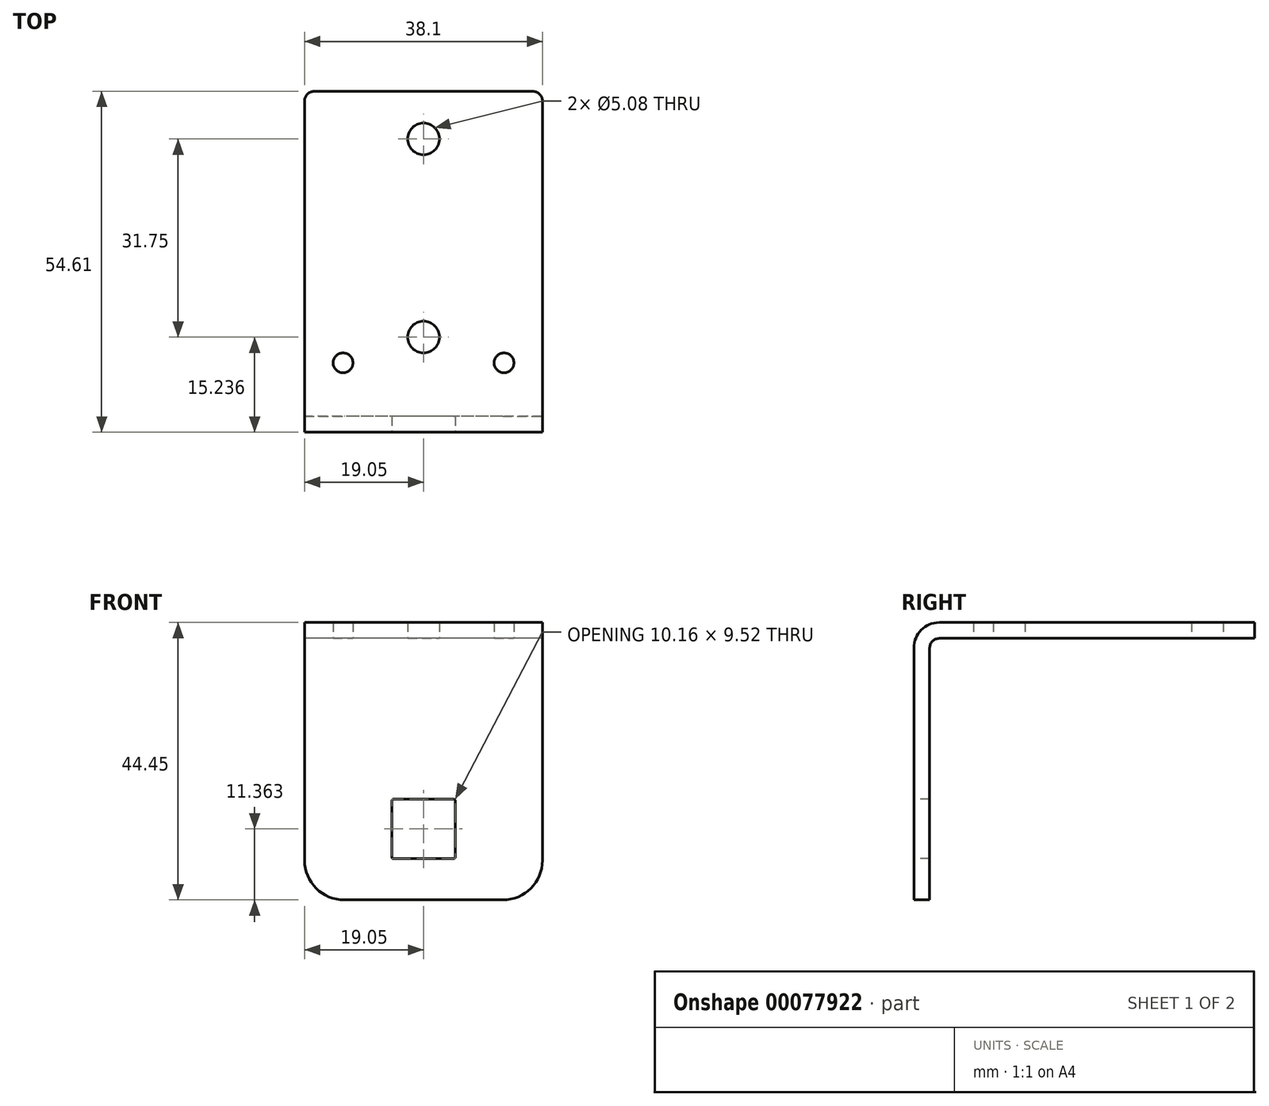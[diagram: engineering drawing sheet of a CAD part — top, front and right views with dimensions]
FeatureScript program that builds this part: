
annotation { "Feature Type Name" : "Feature", "Feature Type Description" : "" }
export const myFeature = defineFeature(function(context is Context, id is Id, definition is map)
    precondition{}
    {
        {
            var Q0;
            Q0=qCreatedBy(makeId("Right.planeOp"),FACE);
            var sketch = newSketch(context, id + "F0", { "sketchPlane" : qUnion([Q0])});
            skLineSegment(sketch, "E0.bottom", {"start": v(-52.32, 1.02) * mm, "end": v(-54.86, 1.02) * mm});
            skLineSegment(sketch, "E0.top", {"start": v(-0.25, 45.47) * mm, "end": v(-50.8, 45.47) * mm});
            skLineSegment(sketch, "E0.left", {"start": v(-0.25, 42.93) * mm, "end": v(-0.25, 45.47) * mm});
            skLineSegment(sketch, "E0.right", {"start": v(-54.86, 1.02) * mm, "end": v(-54.86, 41.4) * mm});
            skLineSegment(sketch, "E1", {"start": v(-52.32, 1.02) * mm, "end": v(-52.32, 41.4) * mm});
            skLineSegment(sketch, "E2", {"start": v(-50.8, 42.93) * mm, "end": v(-0.25, 42.93) * mm});
            skPoint(sketch, "E3.visualSharp", {"position": v(-52.32, 42.93) * mm});
            skArc(sketch, "E3.filletArc", {"start": v(-50.8, 42.93) * mm, "mid": v(-51.88, 42.48) * mm, "end": v(-52.32, 41.4) * mm});
            skPoint(sketch, "E4.visualSharp", {"position": v(-54.86, 45.47) * mm});
            skArc(sketch, "E4.filletArc", {"start": v(-50.8, 45.47) * mm, "mid": v(-53.67, 44.28) * mm, "end": v(-54.86, 41.4) * mm});
            skSolve(sketch);
        }
        {
            var Q0;
            Q0 = qSketchRegion(id + "F0", true);
            extrude(context, id + "F1", {"entities" : qUnion([Q0]), "depth" : 38.1 * mm});
        }
        {
            var Q0;
            Q0=makeQuery(id+"F1.opExtrude","CAP_EDGE",EDGE,{"disambiguationData":[OSD([sQuery(id+"F0.wireOp",EDGE,"E0.left")])],"isStart":true});
            var Q1;
            Q1=makeQuery(id+"F1.opExtrude","CAP_EDGE",EDGE,{"disambiguationData":[OSD([sQuery(id+"F0.wireOp",EDGE,"E0.left")])],"isStart":false});
            fillet(context, id + "F2", {"entities" : qUnion([Q0, Q1]), "radius" : 1.52 * mm, "tangentPropagation" : true, "allowEdgeOverflow" : false});
        }
        {
            var Q0;
            Q0=makeQuery(id+"F1.opExtrude","SWEPT_FACE",FACE,{"disambiguationData":[OSD([sQuery(id+"F0.wireOp",EDGE,"E2")])]});
            var sketch = newSketch(context, id + "F3", { "sketchPlane" : qUnion([Q0])});
            skCircle(sketch, "E5", {"center": v(6.16, 43.75) * mm, "radius": 1.59 * mm});
            skCircle(sketch, "E6", {"center": v(19.05, 39.62) * mm, "radius": 2.54 * mm});
            skCircle(sketch, "E7", {"center": v(31.94, 43.75) * mm, "radius": 1.59 * mm});
            skCircle(sketch, "E8", {"center": v(19.05, 7.87) * mm, "radius": 2.54 * mm});
            skLineSegment(sketch, "E9", {"start": v(19.05, 0.25) * mm, "end": v(19.05, 50.8) * mm, "construction": true});
            skLineSegment(sketch, "E10", {"start": v(0, 43.75) * mm, "end": v(38.1, 43.75) * mm, "construction": true});
            skSolve(sketch);
        }
        {
            var Q0;
            Q0 = qSketchRegion(id + "F3", true);
            extrude(context, id + "F4", {"entities" : qUnion([Q0]), "operationType" : NewBodyOperationType.REMOVE, "endBound" : BoundingType.UP_TO_NEXT, "oppositeDirection" : true, "depth" : 25.4 * mm});
        }
        {
            var Q0;
            Q0=makeQuery(id+"F1.opExtrude","SWEPT_FACE",FACE,{"disambiguationData":[OSD([sQuery(id+"F0.wireOp",EDGE,"E0.right")])]});
            var sketch = newSketch(context, id + "F5", { "sketchPlane" : qUnion([Q0])});
            skLineSegment(sketch, "E11.bottom", {"start": v(14.22, 7.62) * mm, "end": v(23.88, 7.62) * mm});
            skLineSegment(sketch, "E11.top", {"start": v(14.22, 17.15) * mm, "end": v(23.88, 17.15) * mm});
            skLineSegment(sketch, "E11.left", {"start": v(13.97, 7.87) * mm, "end": v(13.97, 16.9) * mm});
            skLineSegment(sketch, "E11.right", {"start": v(24.13, 7.87) * mm, "end": v(24.13, 16.9) * mm});
            skLineSegment(sketch, "E12", {"start": v(19.05, 1.02) * mm, "end": v(19.05, 7.62) * mm, "construction": true});
            skPoint(sketch, "E13.visualSharp", {"position": v(13.97, 17.15) * mm});
            skArc(sketch, "E13.filletArc", {"start": v(14.22, 17.14) * mm, "mid": v(14.04, 17.07) * mm, "end": v(13.97, 16.9) * mm});
            skPoint(sketch, "E14.visualSharp", {"position": v(24.13, 17.15) * mm});
            skArc(sketch, "E14.filletArc", {"start": v(24.13, 16.9) * mm, "mid": v(24.06, 17.07) * mm, "end": v(23.88, 17.15) * mm});
            skPoint(sketch, "E15.visualSharp", {"position": v(24.13, 7.62) * mm});
            skArc(sketch, "E15.filletArc", {"start": v(23.88, 7.62) * mm, "mid": v(24.06, 7.7) * mm, "end": v(24.13, 7.87) * mm});
            skPoint(sketch, "E16.visualSharp", {"position": v(13.97, 7.62) * mm});
            skArc(sketch, "E16.filletArc", {"start": v(13.97, 7.87) * mm, "mid": v(14.04, 7.7) * mm, "end": v(14.22, 7.62) * mm});
            skSolve(sketch);
        }
        {
            var Q0;
            Q0 = qSketchRegion(id + "F5", true);
            extrude(context, id + "F6", {"entities" : qUnion([Q0]), "operationType" : NewBodyOperationType.REMOVE, "endBound" : BoundingType.UP_TO_NEXT, "oppositeDirection" : true, "depth" : 25.4 * mm});
        }
        {
            var Q0;
            Q0=makeQuery(id+"F1.opExtrude","CAP_EDGE",EDGE,{"disambiguationData":[OSD([sQuery(id+"F0.wireOp",EDGE,"E0.bottom")])],"isStart":false});
            var Q1;
            Q1=makeQuery(id+"F1.opExtrude","CAP_EDGE",EDGE,{"disambiguationData":[OSD([sQuery(id+"F0.wireOp",EDGE,"E0.bottom")])],"isStart":true});
            fillet(context, id + "F7", {"entities" : qUnion([Q0, Q1]), "radius" : 6.35 * mm, "tangentPropagation" : true, "allowEdgeOverflow" : false});
        }
    });
